# Revit family: Closet_Support_0250_JRSmith
name_source: partatom
category: Plumbing Fixtures
revit_build: Autodesk Revit MEP 2012 (Build: 20110309_2315(x64)
units: mm (PartAtom-declared; Revit-internal decimal feet)

## types (5) — shared parameters
04 CSI = 22 05 29
95 CSI = 15050
Assembly Code = D2010110
Barrel Height = 23"
Capacity = 300lb
Caulk Connection = Yes
Default Elevation = 0"
Description = Compact Fixture Supports with Vertical Offset Fittings for Siphon Jet Water Closets
Fixture Offset = 0"
Horizantal Barel = 15"
Inlet Pipe Offset = 8 43/64"
LEED = Yes
Lug Offset = 2 93/128"
Manufacturer = Jay R. Smith Mfg. Co.
Material = Cast Iron
No-Hub Connection = Yes
Offset From Base = 9"
OmniClass Code = 22-22 42 13
OmniClass Title = Commercial Water Closets, Urinals, and Bidets
Product URL = http://www.jrsmith.com
SMARTBIM Object Version = 3
SMARTBIM URL = www.smartbim.com
Stud Length = 8"
Technical and Installation = http://www.jrsmith.com
URL = http://www.jrsmith.com
Vent Radius = 1"
Warranty = 1 year material and workmanship
zero-valued in all types: Max.Static Load Lbs

## per-type parameters (varying)
| type | Angled Lug | Barrel Width | E | Inlet Pipe Radius | Inner Radius | Lug Nut Angled | Material Finish | Model | Nipple Length | Pipe Diameter | Pipe Diameter 2 | Pipe Radius-1 | Pipe Radius-2 | Radius | Straight Lug | Top Pipe Radius | Weight (lb) |
| 0250Y-4X4 | Yes | 6" | 10" | 1 1/2" | 1 3/8" | No | Duco coated | 0250DY-6X5 | 9" | 4" | 4" | 2" | 2" | 2" | No | 1" | 0 |
| 0250Y-6X4 | Yes | 6 1/2" | 11 1/2" | 2 1/2" | 2 3/8" | Yes | Duco coated | 0250DY-6X4 | 11 1/2" | 6" | 5" | 3" | 2 1/2" | 2" | No | 1 1/2" | 99.9 |
| 0250Y-5X4 | Yes | 5 1/2" | 11 1/2" | 2" | 1 7/8" | Yes | Duco Coated | 0250DY-5X4 | 11 1/2" | 5" | 4" | 2 1/2" | 2" | 2" | No | 1 1/4" | 102.9 |
| 0250Y-6X5 | No | 6" | 11 1/2" | 2 1/2" | 2 3/8" | No | Duco coated | 0250DY-6X5 | 11 1/2" | 6" | 5" | 3" | 2 1/2" | 2 1/2" | Yes | 1 1/2" | 0 |
| 0250Y-5X5 | No | 5 1/2" | 11 1/2" | 2" | 1 7/8" | Yes | Duco coated | 0250DY-5X5 | 11 1/2" | 5" | 5" | 2 1/2" | 2 1/2" | 2 1/2" | Yes | 1 1/4" | 0 |

## geometry (parser evidence)
native form markers: Blend x6, Sweep x34
no freeform markers — native parametric forms only
